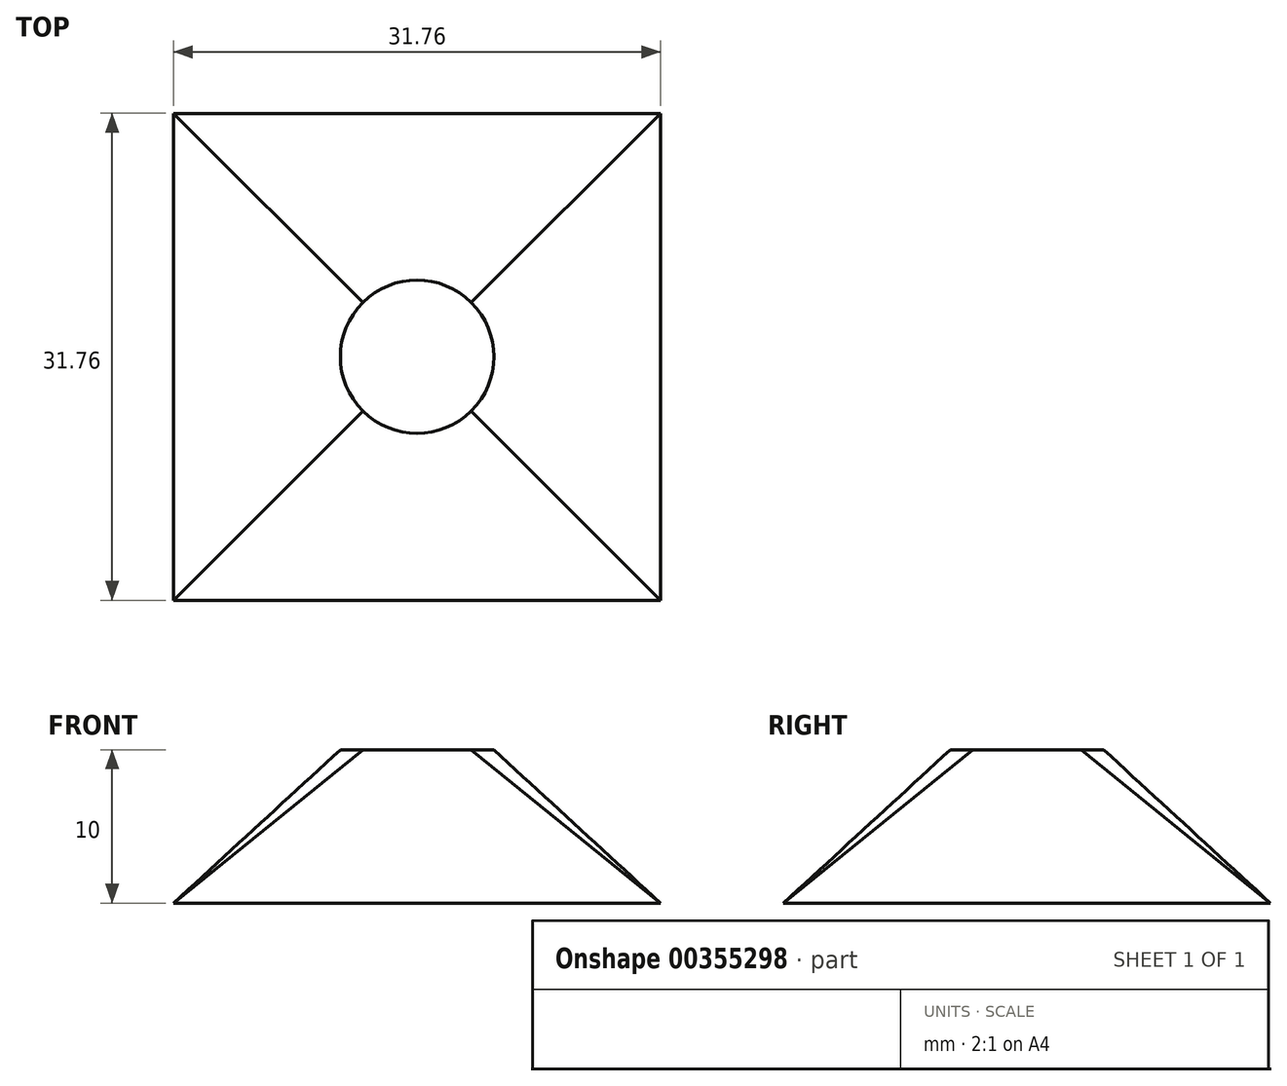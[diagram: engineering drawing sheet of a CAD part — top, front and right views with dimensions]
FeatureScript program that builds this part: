
annotation { "Feature Type Name" : "Feature", "Feature Type Description" : "" }
export const myFeature = defineFeature(function(context is Context, id is Id, definition is map)
    precondition{}
    {
        {
            var Q0;
            Q0=qCreatedBy(makeId("Top.planeOp"),FACE);
            var sketch = newSketch(context, id + "F0", { "sketchPlane" : qUnion([Q0])});
            skLineSegment(sketch, "E0.bottom", {"start": v(-15.87, 15.88) * mm, "end": v(15.88, 15.88) * mm});
            skLineSegment(sketch, "E0.top", {"start": v(-15.88, -15.88) * mm, "end": v(15.87, -15.88) * mm});
            skLineSegment(sketch, "E0.left", {"start": v(-15.87, 15.88) * mm, "end": v(-15.88, -15.88) * mm});
            skLineSegment(sketch, "E0.right", {"start": v(15.88, 15.88) * mm, "end": v(15.87, -15.88) * mm});
            skPoint(sketch, "E0.middle", {"position": v(0, 0) * mm});
            skSolve(sketch);
        }
        {
            var Q0;
            Q0=qCreatedBy(makeId("Top.planeOp"),FACE);
            cPlane(context, id + "F1", {"entities" : qUnion([Q0]), "cplaneType" : CPlaneType.OFFSET, "offset" : 10 * mm, "width" : 150 * mm, "height" : 150 * mm});
        }
        {
            var Q0;
            Q0=qCreatedBy(id+"F1.planeOp",FACE);
            var sketch = newSketch(context, id + "F2", { "sketchPlane" : qUnion([Q0])});
            skCircle(sketch, "E1", {"center": v(0, 0) * mm, "radius": 5 * mm});
            skSolve(sketch);
        }
        {
            var Q0;
            Q0=makeQuery(id+"F0.imprint","IMPRINT",FACE,{"disambiguationData":[TD([[makeQuery(id+"F0.imprint","IMPRINT",EDGE,{"derivedFrom":sQuery(id+"F0.wireOp",EDGE,"E0.bottom")}),-1.0]])]});
            var Q1;
            Q1=makeQuery(id+"F2.imprint","IMPRINT",FACE,{"disambiguationData":[TD([[makeQuery(id+"F2.imprint","IMPRINT",EDGE,{"derivedFrom":sQuery(id+"F2.wireOp",EDGE,"E1")}),1.0]])]});
            loft(context, id + "F3", {"sheetProfilesArray" : [{ "sheetProfileEntities" : qUnion([Q0]) }, { "sheetProfileEntities" : qUnion([Q1]) }]});
        }
    });
